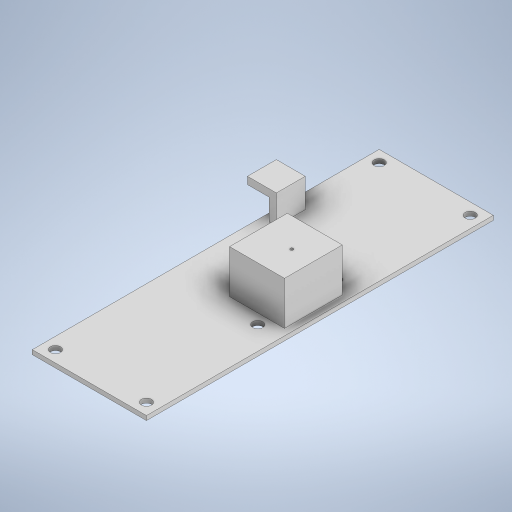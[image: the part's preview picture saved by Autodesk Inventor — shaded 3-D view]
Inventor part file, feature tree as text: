
AUTODESK INVENTOR PART (.ipt)
format: ipt  version: 2023 (Build 270158000, 158)  size: 333,824 bytes
history: native  units: mm
features: extrude x11, sketch x11
ambient origin geometry x8: Origin, YZ Plane, XZ Plane, XY Plane, X Axis, Y Axis, Z Axis, Center Point
bodies: Body1 (feature_tree)
feature tree (22):
  extrude  "Extrusion33"  Depth=240.0mm
  extrude  "Extrusion34"  Depth=3.0mm
  extrude  "Extrusion35"  Depth=30.0mm TaperAngle=0.0deg
  extrude  "Extrusion38"  Depth=30.0mm
  extrude  "Extrusion39"  Depth=15.0mm
  extrude  "Extrusion40"  Depth=15.0mm
  extrude  "Extrusion41"  Depth=35.0mm TaperAngle=0.0deg
  extrude  "Extrusion42"  Depth=20.0mm
  extrude  "Extrusion43"  Depth=20.0mm
  extrude  "Extrusion46"  Depth=5.0mm TaperAngle=0.0deg
  extrude  "Extrusion47"  TaperAngle=0.0deg  [1 undecoded]
  sketch  "Sketch44"  dims[d138=79.0mm d139=240.0mm]
  sketch  "Sketch45"  dims[d140=3.0mm d141=0.0mm d142=38.0mm]
  sketch  "Sketch47"  dims[d143=40.0mm d144=30.0mm d145=0.0mm]
  sketch  "Sketch58"  dims[d146=36.0mm d147=30.0mm d148=-2.617994mm]
  sketch  "Sketch59"  dims[d156=20.0mm d157=15.0mm]
  sketch  "Sketch60"  dims[d158=15.0mm d159=0.0mm d160=3.2mm]
  sketch  "Sketch61"  dims[d161=20.0mm d162=35.0mm d163=0.0mm]
  sketch  "Sketch64"  dims[d164=5.0mm d165=20.0mm]
  sketch  "Sketch65"  dims[d166=20.0mm d167=0.0mm d168=20.0mm]
  sketch  "Sketch68"  dims[d169=20.0mm d170=5.0mm d171=0.0mm]
  sketch  "Sketch69"  dims[d173=2.0mm d174=0.0mm d175=0.0mm d176=6.0mm d177=10.0mm d178=0.0mm d192=7.0mm d193=7.0mm d194=7.0mm d195=7.0mm d196=10.0mm d197=0.0mm d198=7.0mm d199=7.0mm d200=10.0mm d201=0.0mm d49=0.5mm d50=0.872665mm d51=0.5mm d52=0.872665mm d130=0.5mm d131=0.872665mm d132=0.5mm d133=0.872665mm]
note: 1 required parameter value undecoded (feature->parameter linkage not recoverable at this tier; creation-order binding heuristic only, values carry confidence <= 0.55)
